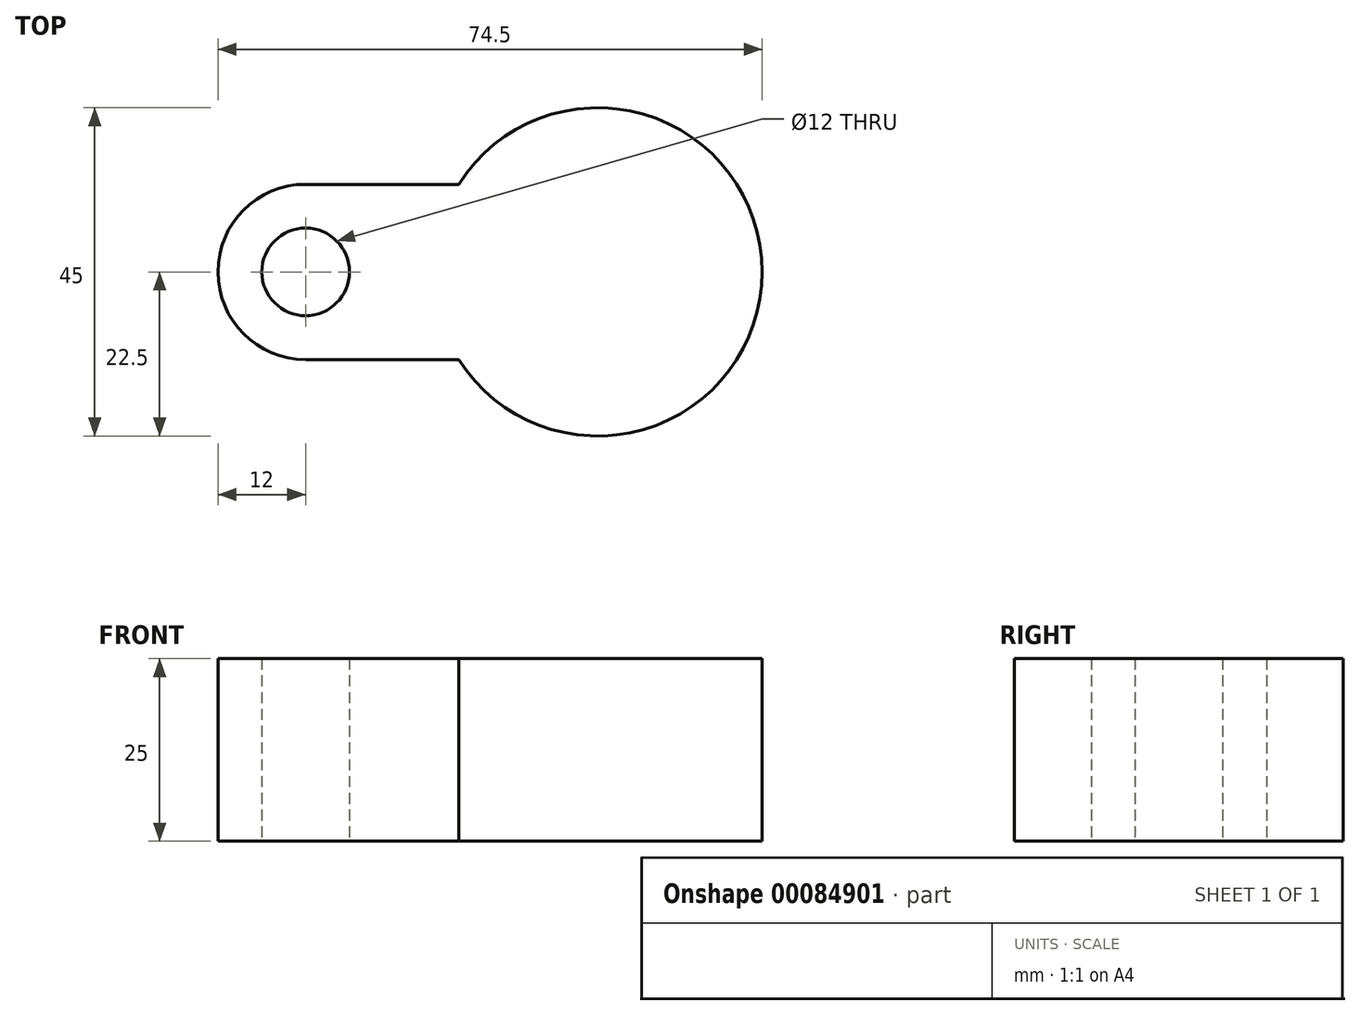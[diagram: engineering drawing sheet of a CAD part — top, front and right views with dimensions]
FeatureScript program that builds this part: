
annotation { "Feature Type Name" : "Feature", "Feature Type Description" : "" }
export const myFeature = defineFeature(function(context is Context, id is Id, definition is map)
    precondition{}
    {
        {
            var Q0;
            Q0=qCreatedBy(makeId("Top.planeOp"),FACE);
            var sketch = newSketch(context, id + "F0", { "sketchPlane" : qUnion([Q0])});
            skCircle(sketch, "E0", {"center": v(0, 0) * mm, "radius": 22.5 * mm});
            skPoint(sketch, "E1", {"position": v(-40, 0) * mm});
            skArc(sketch, "E2", {"start": v(-40, 12) * mm, "mid": v(-52, 0) * mm, "end": v(-40, -12) * mm});
            skLineSegment(sketch, "E3", {"start": v(-40, 12) * mm, "end": v(-19.03, 12) * mm});
            skLineSegment(sketch, "E4", {"start": v(-40, -12) * mm, "end": v(-19.03, -12) * mm});
            skCircle(sketch, "E5", {"center": v(-40, 0) * mm, "radius": 6 * mm});
            skSolve(sketch);
        }
        {
            var Q0;
            Q0 = qSketchRegion(id + "F0", true);
            extrude(context, id + "F1", {"entities" : qUnion([Q0]), "depth" : 25 * mm, "offsetDistance" : 25 * mm});
        }
    });
